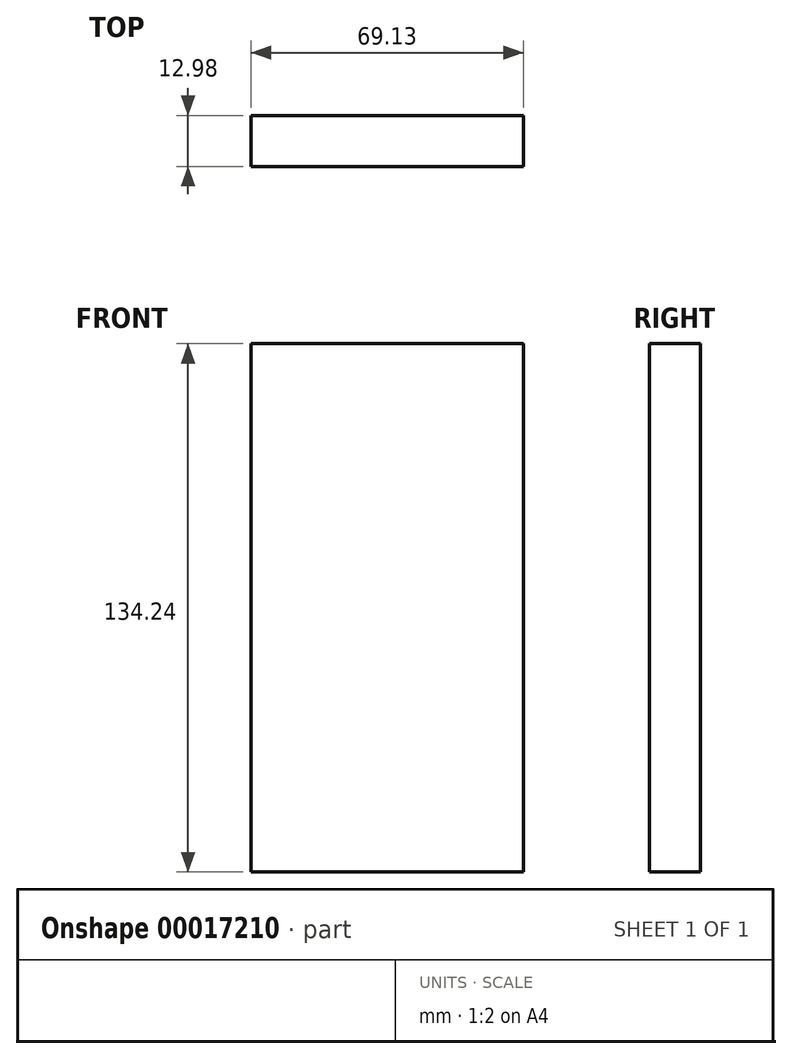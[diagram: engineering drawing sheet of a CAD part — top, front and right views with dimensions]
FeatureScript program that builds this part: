
annotation { "Feature Type Name" : "Feature", "Feature Type Description" : "" }
export const myFeature = defineFeature(function(context is Context, id is Id, definition is map)
    precondition{}
    {
        {
            var Q0;
            Q0=qCreatedBy(makeId("Front.planeOp"),FACE);
            var sketch = newSketch(context, id + "F0", { "sketchPlane" : qUnion([Q0])});
            skLineSegment(sketch, "E0.bottom", {"start": v(-53.84, 74.46) * mm, "end": v(15.3, 74.46) * mm});
            skLineSegment(sketch, "E0.top", {"start": v(-53.84, -60.04) * mm, "end": v(15.3, -60.04) * mm});
            skLineSegment(sketch, "E0.left", {"start": v(-53.84, 74.46) * mm, "end": v(-53.84, -60.04) * mm});
            skLineSegment(sketch, "E0.right", {"start": v(15.3, 74.46) * mm, "end": v(15.3, -60.04) * mm});
            skSolve(sketch);
        }
        {
            var Q0;
            Q0 = qSketchRegion(id + "F0", true);
            extrude(context, id + "F1", {"entities" : qUnion([Q0]), "oppositeDirection" : true, "depth" : 11.56 * mm});
        }
        {
            var Q0;
            Q0=makeQuery(id+"F1.opExtrude","SWEPT_BODY",BODY,{"disambiguationData":[OSD([sQuery(id+"F0.wireOp",EDGE,"E0.bottom"),sQuery(id+"F0.wireOp",EDGE,"E0.top"),sQuery(id+"F0.wireOp",EDGE,"E0.left"),sQuery(id+"F0.wireOp",EDGE,"E0.right")])]});
            deleteBodies(context, id + "F2", {"entities" : qUnion([Q0])});
        }
        {
            var Q0;
            Q0=qCreatedBy(makeId("Front.planeOp"),FACE);
            var sketch = newSketch(context, id + "F3", { "sketchPlane" : qUnion([Q0])});
            skLineSegment(sketch, "E1.bottom", {"start": v(-39.22, 60.89) * mm, "end": v(29.92, 60.89) * mm});
            skLineSegment(sketch, "E1.top", {"start": v(-39.22, -73.6) * mm, "end": v(29.92, -73.6) * mm});
            skLineSegment(sketch, "E1.left", {"start": v(-39.22, 60.89) * mm, "end": v(-39.22, -73.6) * mm});
            skLineSegment(sketch, "E1.right", {"start": v(29.92, 60.89) * mm, "end": v(29.92, -73.6) * mm});
            skSolve(sketch);
        }
        {
            var Q0;
            Q0 = qSketchRegion(id + "F3", true);
            extrude(context, id + "F4", {"entities" : qUnion([Q0]), "depth" : 11.56 * mm});
        }
        {
            var Q0;
            Q0=makeQuery(id+"F4.opExtrude","SWEPT_BODY",BODY,{"disambiguationData":[OSD([sQuery(id+"F3.wireOp",EDGE,"E1.bottom"),sQuery(id+"F3.wireOp",EDGE,"E1.top"),sQuery(id+"F3.wireOp",EDGE,"E1.left"),sQuery(id+"F3.wireOp",EDGE,"E1.right")])]});
            deleteBodies(context, id + "F5", {"entities" : qUnion([Q0])});
        }
        {
            var Q0;
            Q0=qCreatedBy(makeId("Front.planeOp"),FACE);
            var sketch = newSketch(context, id + "F6", { "sketchPlane" : qUnion([Q0])});
            skLineSegment(sketch, "E2.bottom", {"start": v(-59.2, 68.48) * mm, "end": v(9.93, 68.48) * mm});
            skLineSegment(sketch, "E2.top", {"start": v(-59.2, -65.76) * mm, "end": v(9.93, -65.76) * mm});
            skLineSegment(sketch, "E2.left", {"start": v(-59.2, 68.48) * mm, "end": v(-59.2, -65.76) * mm});
            skLineSegment(sketch, "E2.right", {"start": v(9.93, 68.48) * mm, "end": v(9.93, -65.76) * mm});
            skSolve(sketch);
        }
        {
            var Q0;
            Q0=makeQuery(id+"F6.imprint","IMPRINT",FACE,{"disambiguationData":[TD([[makeQuery(id+"F6.imprint","IMPRINT",EDGE,{"derivedFrom":sQuery(id+"F6.wireOp",EDGE,"E2.bottom")}),-1.0]])]});
            extrude(context, id + "F7", {"entities" : qUnion([Q0]), "depth" : 12.98 * mm});
        }
    });
